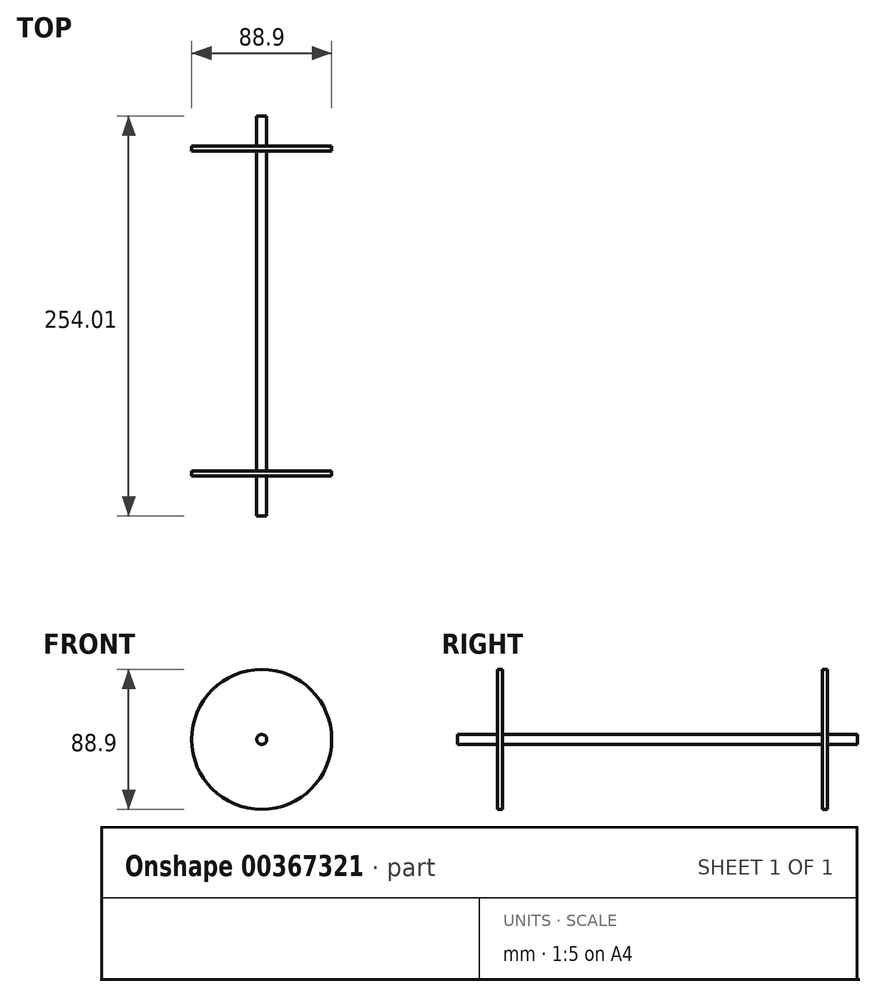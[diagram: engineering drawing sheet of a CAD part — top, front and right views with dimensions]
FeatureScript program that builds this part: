
annotation { "Feature Type Name" : "Feature", "Feature Type Description" : "" }
export const myFeature = defineFeature(function(context is Context, id is Id, definition is map)
    precondition{}
    {
        {
            var Q0;
            Q0=qCreatedBy(makeId("Front.planeOp"),FACE);
            var sketch = newSketch(context, id + "F0", { "sketchPlane" : qUnion([Q0])});
            skCircle(sketch, "E0", {"center": v(0, 0) * mm, "radius": 3.18 * mm});
            skSolve(sketch);
        }
        {
            var Q0;
            Q0 = qSketchRegion(id + "F0", true);
            extrude(context, id + "F1", {"entities" : qUnion([Q0]), "depth" : 203.2 * mm});
        }
        {
            var Q0;
            Q0=makeQuery(id+"F1.opExtrude","CAP_FACE",FACE,{"disambiguationData":[OSD([sQuery(id+"F0.wireOp",EDGE,"E0")])],"isStart":false});
            var sketch = newSketch(context, id + "F2", { "sketchPlane" : qUnion([Q0])});
            skCircle(sketch, "E1", {"center": v(0, 0) * mm, "radius": 44.45 * mm});
            skSolve(sketch);
        }
        {
            var Q0;
            Q0 = qSketchRegion(id + "F2", true);
            extrude(context, id + "F3", {"entities" : qUnion([Q0]), "operationType" : NewBodyOperationType.ADD, "depth" : 3.17 * mm});
        }
        {
            var Q0;
            Q0=makeQuery(id+"F1.opExtrude","CAP_FACE",FACE,{"disambiguationData":[OSD([sQuery(id+"F0.wireOp",EDGE,"E0")])],"isStart":true});
            var sketch = newSketch(context, id + "F4", { "sketchPlane" : qUnion([Q0])});
            skCircle(sketch, "E2", {"center": v(0, 0) * mm, "radius": 44.45 * mm});
            skSolve(sketch);
        }
        {
            var Q0;
            Q0 = qSketchRegion(id + "F4", true);
            extrude(context, id + "F5", {"entities" : qUnion([Q0]), "operationType" : NewBodyOperationType.ADD, "depth" : 3.17 * mm});
        }
        {
            var Q0;
            Q0=makeQuery(id+"F3.opExtrude","CAP_FACE",FACE,{"disambiguationData":[OSD([sQuery(id+"F2.wireOp",EDGE,"E1")])],"isStart":false});
            var sketch = newSketch(context, id + "F6", { "sketchPlane" : qUnion([Q0])});
            skCircle(sketch, "E3", {"center": v(0, 0) * mm, "radius": 3.18 * mm});
            skSolve(sketch);
        }
        {
            var Q0;
            Q0 = qSketchRegion(id + "F6", true);
            extrude(context, id + "F7", {"entities" : qUnion([Q0]), "operationType" : NewBodyOperationType.ADD, "depth" : 25.4 * mm});
        }
        {
            var Q0;
            Q0=makeQuery(id+"F5.opExtrude","CAP_FACE",FACE,{"disambiguationData":[OSD([sQuery(id+"F4.wireOp",EDGE,"E2")])],"isStart":false});
            var sketch = newSketch(context, id + "F8", { "sketchPlane" : qUnion([Q0])});
            skCircle(sketch, "E4", {"center": v(0, 0) * mm, "radius": 3.18 * mm});
            skSolve(sketch);
        }
        {
            var Q0;
            Q0 = qSketchRegion(id + "F8", true);
            extrude(context, id + "F9", {"entities" : qUnion([Q0]), "operationType" : NewBodyOperationType.ADD, "depth" : 19.05 * mm});
        }
    });
